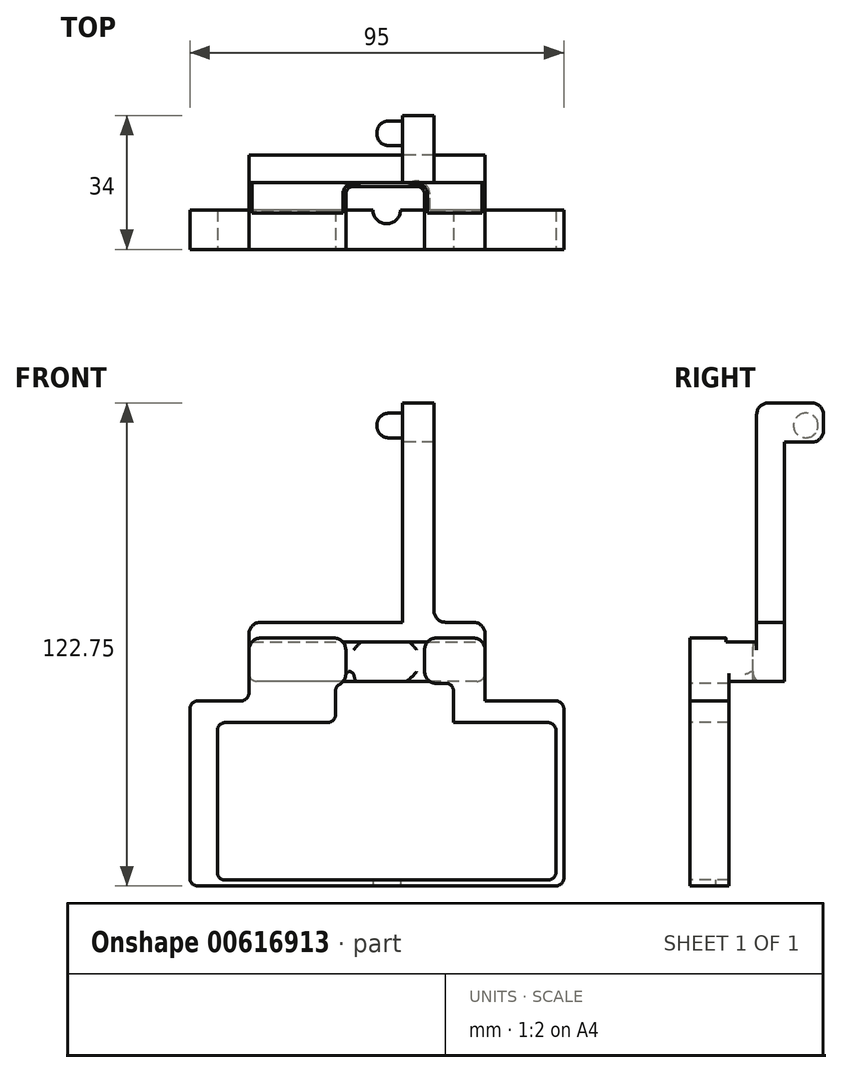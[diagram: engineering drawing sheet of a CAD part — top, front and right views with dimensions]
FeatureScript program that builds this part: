
annotation { "Feature Type Name" : "Feature", "Feature Type Description" : "" }
export const myFeature = defineFeature(function(context is Context, id is Id, definition is map)
    precondition{}
    {
        {
            var Q0;
            Q0=qCreatedBy(makeId("Front.planeOp"),FACE);
            var sketch = newSketch(context, id + "F0", { "sketchPlane" : qUnion([Q0])});
            skLineSegment(sketch, "E0.bottom", {"start": v(47.5, -23.5) * mm, "end": v(-47.5, -23.5) * mm});
            skLineSegment(sketch, "E0.top", {"start": v(47.5, 23.5) * mm, "end": v(-47.5, 23.5) * mm});
            skLineSegment(sketch, "E0.left", {"start": v(47.5, -23.5) * mm, "end": v(47.5, 23.5) * mm});
            skLineSegment(sketch, "E0.right", {"start": v(-47.5, -23.5) * mm, "end": v(-47.5, 23.5) * mm});
            skPoint(sketch, "E0.middle", {"position": v(0, 0) * mm});
            skSolve(sketch);
        }
        {
            var Q0;
            Q0=makeQuery(id+"F0.imprint","IMPRINT",FACE,{"disambiguationData":[TD([[makeQuery(id+"F0.imprint","IMPRINT",EDGE,{"derivedFrom":sQuery(id+"F0.wireOp",EDGE,"E0.bottom")}),-1.0]])]});
            extrude(context, id + "F1", {"entities" : qUnion([Q0]), "depth" : 1 * mm, "offsetDistance" : 25 * mm});
        }
        {
            var Q0;
            Q0=makeQuery(id+"F1.opExtrude","CAP_FACE",FACE,{"disambiguationData":[OSD([sQuery(id+"F0.wireOp",EDGE,"E0.bottom"),sQuery(id+"F0.wireOp",EDGE,"E0.top"),sQuery(id+"F0.wireOp",EDGE,"E0.left"),sQuery(id+"F0.wireOp",EDGE,"E0.right")])],"isStart":false});
            var sketch = newSketch(context, id + "F2", { "sketchPlane" : qUnion([Q0])});
            skLineSegment(sketch, "E1.bottom", {"start": v(-40.5, 18) * mm, "end": v(45.5, 18) * mm});
            skLineSegment(sketch, "E1.top", {"start": v(-40.5, -22) * mm, "end": v(45.5, -22) * mm});
            skLineSegment(sketch, "E1.left", {"start": v(-40.5, 18) * mm, "end": v(-40.5, -22) * mm});
            skLineSegment(sketch, "E1.right", {"start": v(45.5, 18) * mm, "end": v(45.5, -22) * mm});
            skLineSegment(sketch, "E2", {"start": v(2.5, -22) * mm, "end": v(2.5, -23.5) * mm});
            skLineSegment(sketch, "E3", {"start": v(45.5, 0) * mm, "end": v(47.5, 0) * mm});
            skLineSegment(sketch, "E4", {"start": v(-40.5, 0) * mm, "end": v(-47.5, 0) * mm});
            skLineSegment(sketch, "E5", {"start": v(32.76, 23.5) * mm, "end": v(32.76, 18) * mm});
            skSolve(sketch);
        }
        {
            var Q0;
            {var subQ4=sQuery(id+"F2.wireOp",EDGE,"E1.left");var subQ6=sQuery(id+"F2.wireOp",EDGE,"E1.bottom");var subQ9=makeQuery(id+"F2.imprint","INTERSECT",VERTEX,{"derivedFrom":[subQ6,subQ4]});Q0=makeQuery(id+"F2.imprint","IMPRINT",FACE,{"disambiguationData":[TD([[makeQuery(id+"F2.imprint","IMPRINT",EDGE,{"disambiguationData":[TD([[subQ9,-1.0]])],"derivedFrom":subQ6}),-1.0]])]});}
            extrude(context, id + "F3", {"entities" : qUnion([Q0]), "operationType" : NewBodyOperationType.REMOVE, "oppositeDirection" : true, "depth" : 25 * mm, "offsetDistance" : 25 * mm});
        }
        {
            var Q0;
            Q0=makeQuery(id+"F1.opExtrude","SWEPT_FACE",FACE,{"disambiguationData":[OSD([sQuery(id+"F0.wireOp",EDGE,"E0.top")])]});
            var sketch = newSketch(context, id + "F4", { "sketchPlane" : qUnion([Q0])});
            skLineSegment(sketch, "E6.bottom", {"start": v(27.5, 0) * mm, "end": v(-32.5, 0) * mm});
            skLineSegment(sketch, "E6.top", {"start": v(27.5, -1) * mm, "end": v(-32.5, -1) * mm});
            skLineSegment(sketch, "E6.left", {"start": v(27.5, 0) * mm, "end": v(27.5, -1) * mm});
            skLineSegment(sketch, "E6.right", {"start": v(-32.5, 0) * mm, "end": v(-32.5, -1) * mm});
            skLineSegment(sketch, "E7", {"start": v(47.5, -0.5) * mm, "end": v(27.5, -0.5) * mm});
            skSolve(sketch);
        }
        {
            var Q0;
            {var subQ4=sQuery(id+"F4.wireOp",EDGE,"E6.bottom");Q0=makeQuery(id+"F4.imprint","IMPRINT",FACE,{"disambiguationData":[TD([[makeQuery(id+"F4.imprint","IMPRINT",EDGE,{"derivedFrom":subQ4}),1.0]])]});}
            extrude(context, id + "F5", {"entities" : qUnion([Q0]), "operationType" : NewBodyOperationType.ADD, "depth" : 15 * mm, "offsetDistance" : 25 * mm});
        }
        {
            var Q0;
            Q0=makeQuery(id+"F5.boolean.opBoolean","MERGE",FACE,{"derivedFrom":[makeQuery(id+"F1.opExtrude","CAP_FACE",FACE,{"disambiguationData":[OSD([sQuery(id+"F0.wireOp",EDGE,"E0.bottom"),sQuery(id+"F0.wireOp",EDGE,"E0.top"),sQuery(id+"F0.wireOp",EDGE,"E0.left"),sQuery(id+"F0.wireOp",EDGE,"E0.right")])],"isStart":false}),makeQuery(id+"F5.opExtrude","SWEPT_FACE",FACE,{"disambiguationData":[OSD([sQuery(id+"F4.wireOp",EDGE,"E6.top")])]})]});
            var sketch = newSketch(context, id + "F6", { "sketchPlane" : qUnion([Q0])});
            skLineSegment(sketch, "E8.bottom", {"start": v(-10.5, 28) * mm, "end": v(19.5, 28) * mm});
            skLineSegment(sketch, "E8.top", {"start": v(-10.5, 18) * mm, "end": v(19.5, 18) * mm});
            skLineSegment(sketch, "E8.left", {"start": v(-10.5, 28) * mm, "end": v(-10.5, 18) * mm});
            skLineSegment(sketch, "E8.right", {"start": v(19.5, 28) * mm, "end": v(19.5, 18) * mm});
            skLineSegment(sketch, "E9", {"start": v(19.5, 26) * mm, "end": v(27.5, 26) * mm});
            skLineSegment(sketch, "E10", {"start": v(23.5, 26) * mm, "end": v(23.5, 18) * mm});
            skLineSegment(sketch, "E11", {"start": v(27.5, 23.5) * mm, "end": v(27.5, 18) * mm});
            skLineSegment(sketch, "E12.bottom", {"start": v(27.5, 39.25) * mm, "end": v(-32.5, 39.25) * mm});
            skLineSegment(sketch, "E12.top", {"start": v(27.5, 29.25) * mm, "end": v(-32.5, 29.25) * mm});
            skLineSegment(sketch, "E12.left", {"start": v(27.5, 39.25) * mm, "end": v(27.5, 29.25) * mm});
            skLineSegment(sketch, "E12.right", {"start": v(-32.5, 39.25) * mm, "end": v(-32.5, 29.25) * mm});
            skSolve(sketch);
        }
        {
            var Q0;
            {var subQ1=sQuery(id+"F6.wireOp",EDGE,"E8.bottom");Q0=makeQuery(id+"F6.imprint","IMPRINT",FACE,{"disambiguationData":[TD([[makeQuery(id+"F6.imprint","IMPRINT",EDGE,{"derivedFrom":subQ1}),-1.0]])]});}
            extrude(context, id + "F7", {"entities" : qUnion([Q0]), "operationType" : NewBodyOperationType.REMOVE, "oppositeDirection" : true, "depth" : 25 * mm, "offsetDistance" : 25 * mm});
        }
        {
            var Q0;
            Q0=makeQuery(id+"F6.imprint","IMPRINT",FACE,{"disambiguationData":[TD([[makeQuery(id+"F6.imprint","IMPRINT",EDGE,{"derivedFrom":sQuery(id+"F6.wireOp",EDGE,"E12.bottom")}),1.0]])]});
            extrude(context, id + "F8", {"entities" : qUnion([Q0]), "operationType" : NewBodyOperationType.REMOVE, "depth" : 2 * mm, "offsetDistance" : 25 * mm});
        }
        {
            var Q0;
            Q0=makeQuery(id+"F3.boolean.opBoolean","COPY",EDGE,{"derivedFrom":makeQuery(id+"F3.opExtrude","SWEPT_EDGE",EDGE,{"disambiguationData":[OSD([sQuery(id+"F2.wireOp",EDGE,"E1.top"),sQuery(id+"F2.wireOp",EDGE,"E1.left")])]})});
            var Q1;
            Q1=makeQuery(id+"F3.boolean.opBoolean","COPY",EDGE,{"derivedFrom":makeQuery(id+"F3.opExtrude","SWEPT_EDGE",EDGE,{"disambiguationData":[OSD([sQuery(id+"F2.wireOp",EDGE,"E1.top"),sQuery(id+"F2.wireOp",EDGE,"E1.right")])]})});
            var Q2;
            Q2=makeQuery(id+"F3.boolean.opBoolean","COPY",EDGE,{"derivedFrom":makeQuery(id+"F3.opExtrude","SWEPT_EDGE",EDGE,{"disambiguationData":[OSD([sQuery(id+"F2.wireOp",EDGE,"E1.bottom"),sQuery(id+"F2.wireOp",EDGE,"E1.right")])]})});
            var Q3;
            Q3=makeQuery(id+"F3.boolean.opBoolean","COPY",EDGE,{"derivedFrom":makeQuery(id+"F3.opExtrude","SWEPT_EDGE",EDGE,{"disambiguationData":[OSD([sQuery(id+"F2.wireOp",EDGE,"E1.bottom"),sQuery(id+"F2.wireOp",EDGE,"E1.left")])]})});
            var Q4;
            Q4=makeQuery(id+"F1.opExtrude","SWEPT_EDGE",EDGE,{"disambiguationData":[OSD([sQuery(id+"F0.wireOp",EDGE,"E0.bottom"),sQuery(id+"F0.wireOp",EDGE,"E0.right")])]});
            var Q5;
            Q5=makeQuery(id+"F1.opExtrude","SWEPT_EDGE",EDGE,{"disambiguationData":[OSD([sQuery(id+"F0.wireOp",EDGE,"E0.bottom"),sQuery(id+"F0.wireOp",EDGE,"E0.left")])]});
            var Q6;
            Q6=makeQuery(id+"F1.opExtrude","SWEPT_EDGE",EDGE,{"disambiguationData":[OSD([sQuery(id+"F0.wireOp",EDGE,"E0.top"),sQuery(id+"F0.wireOp",EDGE,"E0.right")])]});
            var Q7;
            Q7=makeQuery(id+"F5.opExtrude","CAP_EDGE",EDGE,{"disambiguationData":[OSD([sQuery(id+"F4.wireOp",EDGE,"E6.right")])],"isStart":true});
            var Q8;
            Q8=makeQuery(id+"F5.opExtrude","CAP_EDGE",EDGE,{"disambiguationData":[OSD([sQuery(id+"F4.wireOp",EDGE,"E6.left")])],"isStart":true});
            var Q9;
            Q9=makeQuery(id+"F1.opExtrude","SWEPT_EDGE",EDGE,{"disambiguationData":[OSD([sQuery(id+"F0.wireOp",EDGE,"E0.top"),sQuery(id+"F0.wireOp",EDGE,"E0.left")])]});
            var Q10;
            Q10=makeQuery(id+"F7.boolean.opBoolean","COPY",EDGE,{"derivedFrom":makeQuery(id+"F7.opExtrude","SWEPT_EDGE",EDGE,{"disambiguationData":[OSD([sQuery(id+"F2.wireOp",EDGE,"E1.bottom"),sQuery(id+"F6.wireOp",EDGE,"E8.top"),sQuery(id+"F6.wireOp",EDGE,"E8.left")])]})});
            var Q11;
            Q11=makeQuery(id+"F7.boolean.opBoolean","COPY",EDGE,{"derivedFrom":makeQuery(id+"F7.opExtrude","SWEPT_EDGE",EDGE,{"disambiguationData":[OSD([sQuery(id+"F6.wireOp",EDGE,"E8.bottom"),sQuery(id+"F6.wireOp",EDGE,"E8.left")])]})});
            var Q12;
            Q12=makeQuery(id+"F7.boolean.opBoolean","COPY",EDGE,{"derivedFrom":makeQuery(id+"F7.opExtrude","SWEPT_EDGE",EDGE,{"disambiguationData":[OSD([sQuery(id+"F2.wireOp",EDGE,"E1.bottom"),sQuery(id+"F6.wireOp",EDGE,"E8.top"),sQuery(id+"F6.wireOp",EDGE,"E8.right")])]})});
            var Q13;
            Q13=makeQuery(id+"F7.boolean.opBoolean","COPY",EDGE,{"derivedFrom":makeQuery(id+"F7.opExtrude","SWEPT_EDGE",EDGE,{"disambiguationData":[OSD([sQuery(id+"F6.wireOp",EDGE,"E8.bottom"),sQuery(id+"F6.wireOp",EDGE,"E8.right")])]})});
            fillet(context, id + "F9", {"entities" : qUnion([Q0, Q1, Q2, Q3, Q4, Q5, Q6, Q7, Q8, Q9, Q10, Q11, Q12, Q13]), "radius" : 2 * mm, "tangentPropagation" : true, "allowEdgeOverflow" : false});
        }
        {
            var Q0;
            Q0=makeQuery(id+"F5.boolean.opBoolean","MERGE",FACE,{"derivedFrom":[makeQuery(id+"F1.opExtrude","CAP_FACE",FACE,{"disambiguationData":[OSD([sQuery(id+"F0.wireOp",EDGE,"E0.bottom"),sQuery(id+"F0.wireOp",EDGE,"E0.top"),sQuery(id+"F0.wireOp",EDGE,"E0.left"),sQuery(id+"F0.wireOp",EDGE,"E0.right")])],"isStart":true}),makeQuery(id+"F5.opExtrude","SWEPT_FACE",FACE,{"disambiguationData":[OSD([sQuery(id+"F4.wireOp",EDGE,"E6.bottom")])]})]});
            var sketch = newSketch(context, id + "F10", { "sketchPlane" : qUnion([Q0])});
            skLineSegment(sketch, "E13.bottom", {"start": v(-27.5, 38.5) * mm, "end": v(32.5, 38.5) * mm});
            skLineSegment(sketch, "E13.top", {"start": v(-27.5, 28.5) * mm, "end": v(32.5, 28.5) * mm});
            skLineSegment(sketch, "E13.left", {"start": v(-27.5, 38.5) * mm, "end": v(-27.5, 28.5) * mm});
            skLineSegment(sketch, "E13.right", {"start": v(32.5, 38.5) * mm, "end": v(32.5, 28.5) * mm});
            skSolve(sketch);
        }
        {
            var Q0;
            Q0=makeQuery(id+"F10.imprint","IMPRINT",FACE,{"disambiguationData":[TD([[makeQuery(id+"F10.imprint","IMPRINT",EDGE,{"derivedFrom":sQuery(id+"F10.wireOp",EDGE,"E13.bottom")}),-1.0]])]});
            extrude(context, id + "F11", {"entities" : qUnion([Q0]), "operationType" : NewBodyOperationType.ADD, "depth" : 14 * mm, "offsetDistance" : 25 * mm});
        }
        {
            var Q0;
            Q0=makeQuery(id+"F11.boolean.opBoolean","MERGE",FACE,{"derivedFrom":[makeQuery(id+"F5.opExtrude","CAP_FACE",FACE,{"disambiguationData":[OSD([sQuery(id+"F4.wireOp",EDGE,"E6.bottom"),sQuery(id+"F4.wireOp",EDGE,"E6.top"),sQuery(id+"F4.wireOp",EDGE,"E6.left"),sQuery(id+"F4.wireOp",EDGE,"E6.right")])],"isStart":false}),makeQuery(id+"F11.opExtrude","SWEPT_FACE",FACE,{"disambiguationData":[OSD([sQuery(id+"F10.wireOp",EDGE,"E13.bottom")])]})]});
            var sketch = newSketch(context, id + "F12", { "sketchPlane" : qUnion([Q0])});
            skLineSegment(sketch, "E14.bottom", {"start": v(12.12, -1) * mm, "end": v(-7.88, -1) * mm});
            skLineSegment(sketch, "E14.top", {"start": v(12.12, 6) * mm, "end": v(-7.88, 6) * mm});
            skLineSegment(sketch, "E14.left", {"start": v(12.12, -1) * mm, "end": v(12.12, 6) * mm});
            skLineSegment(sketch, "E14.right", {"start": v(-7.88, -1) * mm, "end": v(-7.88, 6) * mm});
            skSolve(sketch);
        }
        {
            var Q0;
            Q0=makeQuery(id+"F12.imprint","IMPRINT",FACE,{"disambiguationData":[TD([[makeQuery(id+"F12.imprint","IMPRINT",EDGE,{"derivedFrom":sQuery(id+"F12.wireOp",EDGE,"E14.bottom")}),-1.0]])]});
            extrude(context, id + "F13", {"entities" : qUnion([Q0]), "operationType" : NewBodyOperationType.REMOVE, "oppositeDirection" : true, "depth" : 25 * mm, "offsetDistance" : 25 * mm});
        }
        {
            var Q0;
            Q0=makeQuery(id+"F11.opExtrude","SWEPT_EDGE",EDGE,{"disambiguationData":[OSD([sQuery(id+"F0.wireOp",EDGE,"E0.bottom"),sQuery(id+"F0.wireOp",EDGE,"E0.top"),sQuery(id+"F0.wireOp",EDGE,"E0.left"),sQuery(id+"F0.wireOp",EDGE,"E0.right"),sQuery(id+"F4.wireOp",EDGE,"E6.bottom"),sQuery(id+"F6.wireOp",EDGE,"E8.right"),sQuery(id+"F10.wireOp",EDGE,"E13.top")])]});
            var Q1;
            Q1=makeQuery(id+"F11.opExtrude","SWEPT_EDGE",EDGE,{"disambiguationData":[OSD([sQuery(id+"F0.wireOp",EDGE,"E0.bottom"),sQuery(id+"F0.wireOp",EDGE,"E0.top"),sQuery(id+"F0.wireOp",EDGE,"E0.left"),sQuery(id+"F0.wireOp",EDGE,"E0.right"),sQuery(id+"F4.wireOp",EDGE,"E6.bottom"),sQuery(id+"F6.wireOp",EDGE,"E8.left"),sQuery(id+"F10.wireOp",EDGE,"E13.top")])]});
            var Q2;
            Q2=makeQuery(id+"F11.opExtrude","SWEPT_EDGE",EDGE,{"disambiguationData":[OSD([sQuery(id+"F10.wireOp",EDGE,"E13.top"),sQuery(id+"F10.wireOp",EDGE,"E13.right")])]});
            var Q3;
            Q3=makeQuery(id+"F11.opExtrude","SWEPT_EDGE",EDGE,{"disambiguationData":[OSD([sQuery(id+"F10.wireOp",EDGE,"E13.top"),sQuery(id+"F10.wireOp",EDGE,"E13.left")])]});
            var Q4;
            Q4=makeQuery(id+"F13.boolean.opBoolean","COPY",EDGE,{"derivedFrom":makeQuery(id+"F13.opExtrude","SWEPT_EDGE",EDGE,{"disambiguationData":[OSD([sQuery(id+"F12.wireOp",EDGE,"E14.top"),sQuery(id+"F12.wireOp",EDGE,"E14.left")])]})});
            var Q5;
            Q5=makeQuery(id+"F13.boolean.opBoolean","COPY",EDGE,{"derivedFrom":makeQuery(id+"F13.opExtrude","SWEPT_EDGE",EDGE,{"disambiguationData":[OSD([sQuery(id+"F12.wireOp",EDGE,"E14.top"),sQuery(id+"F12.wireOp",EDGE,"E14.right")])]})});
            fillet(context, id + "F14", {"entities" : qUnion([Q0, Q1, Q2, Q3, Q4, Q5]), "radius" : 2 * mm, "tangentPropagation" : true, "allowEdgeOverflow" : false});
        }
        {
            var Q0;
            Q0=makeQuery(id+"F11.boolean.opBoolean","MERGE",FACE,{"derivedFrom":[makeQuery(id+"F5.opExtrude","CAP_FACE",FACE,{"disambiguationData":[OSD([sQuery(id+"F4.wireOp",EDGE,"E6.bottom"),sQuery(id+"F4.wireOp",EDGE,"E6.top"),sQuery(id+"F4.wireOp",EDGE,"E6.left"),sQuery(id+"F4.wireOp",EDGE,"E6.right")])],"isStart":false}),makeQuery(id+"F11.opExtrude","SWEPT_FACE",FACE,{"disambiguationData":[OSD([sQuery(id+"F10.wireOp",EDGE,"E13.bottom")])]})]});
            var sketch = newSketch(context, id + "F15", { "sketchPlane" : qUnion([Q0])});
            skLineSegment(sketch, "E15", {"start": v(-32.5, 3.2) * mm, "end": v(1.5, 3.2) * mm});
            skLineSegment(sketch, "E16.bottom", {"start": v(-32.5, -1) * mm, "end": v(-7.88, -1) * mm});
            skLineSegment(sketch, "E16.top", {"start": v(-32.5, 0) * mm, "end": v(-7.88, 0) * mm});
            skLineSegment(sketch, "E16.left", {"start": v(-32.5, -1) * mm, "end": v(-32.5, 0) * mm});
            skLineSegment(sketch, "E16.right", {"start": v(-7.88, -1) * mm, "end": v(-7.88, 0) * mm});
            skLineSegment(sketch, "E17.bottom", {"start": v(12.12, -1) * mm, "end": v(27.5, -1) * mm});
            skLineSegment(sketch, "E17.top", {"start": v(12.12, 0) * mm, "end": v(27.5, 0) * mm});
            skLineSegment(sketch, "E17.left", {"start": v(12.12, -1) * mm, "end": v(12.12, 0) * mm});
            skLineSegment(sketch, "E17.right", {"start": v(27.5, -1) * mm, "end": v(27.5, 0) * mm});
            skLineSegment(sketch, "E18", {"start": v(-32.5, 0) * mm, "end": v(-32.5, 7) * mm});
            skLineSegment(sketch, "E19.bottom", {"start": v(-32.5, 7) * mm, "end": v(27.5, 7) * mm});
            skLineSegment(sketch, "E19.top", {"start": v(-32.5, 14) * mm, "end": v(27.5, 14) * mm});
            skLineSegment(sketch, "E19.left", {"start": v(-32.5, 7) * mm, "end": v(-32.5, 14) * mm});
            skLineSegment(sketch, "E19.right", {"start": v(27.5, 7) * mm, "end": v(27.5, 14) * mm});
            skSolve(sketch);
        }
        {
            var Q0;
            Q0=makeQuery(id+"F15.imprint","IMPRINT",FACE,{"disambiguationData":[TD([[makeQuery(id+"F15.imprint","IMPRINT",EDGE,{"derivedFrom":sQuery(id+"F15.wireOp",EDGE,"E17.bottom")}),-1.0]])]});
            var Q1;
            Q1=makeQuery(id+"F15.imprint","IMPRINT",FACE,{"disambiguationData":[TD([[makeQuery(id+"F15.imprint","IMPRINT",EDGE,{"derivedFrom":sQuery(id+"F15.wireOp",EDGE,"E16.bottom")}),-1.0]])]});
            extrude(context, id + "F16", {"entities" : qUnion([Q0, Q1]), "operationType" : NewBodyOperationType.ADD, "depth" : 1 * mm, "offsetDistance" : 25 * mm});
        }
        {
            var Q0;
            Q0=makeQuery(id+"F15.imprint","IMPRINT",FACE,{"disambiguationData":[TD([[makeQuery(id+"F15.imprint","IMPRINT",EDGE,{"derivedFrom":sQuery(id+"F15.wireOp",EDGE,"E19.bottom")}),1.0]])]});
            extrude(context, id + "F17", {"entities" : qUnion([Q0]), "operationType" : NewBodyOperationType.ADD, "depth" : 5 * mm, "offsetDistance" : 25 * mm});
        }
        {
            var Q0;
            Q0=makeQuery(id+"F17.opExtrude","CAP_FACE",FACE,{"disambiguationData":[OSD([sQuery(id+"F15.wireOp",EDGE,"E19.bottom"),sQuery(id+"F15.wireOp",EDGE,"E19.top"),sQuery(id+"F15.wireOp",EDGE,"E19.left"),sQuery(id+"F15.wireOp",EDGE,"E19.right")])],"isStart":false});
            var sketch = newSketch(context, id + "F18", { "sketchPlane" : qUnion([Q0])});
            skLineSegment(sketch, "E20.bottom", {"start": v(6.5, 14) * mm, "end": v(14.5, 14) * mm});
            skLineSegment(sketch, "E20.top", {"start": v(6.5, 7) * mm, "end": v(14.5, 7) * mm});
            skLineSegment(sketch, "E20.left", {"start": v(6.5, 14) * mm, "end": v(6.5, 7) * mm});
            skLineSegment(sketch, "E20.right", {"start": v(14.5, 14) * mm, "end": v(14.5, 7) * mm});
            skLineSegment(sketch, "E21", {"start": v(-32.5, 10.5) * mm, "end": v(6.5, 10.5) * mm});
            skLineSegment(sketch, "E22", {"start": v(6.5, 10.5) * mm, "end": v(14.5, 10.5) * mm});
            skSolve(sketch);
        }
        {
            var Q0;
            {var subQ0=sQuery(id+"F18.wireOp",EDGE,"E20.top");Q0=makeQuery(id+"F18.imprint","IMPRINT",FACE,{"disambiguationData":[TD([[makeQuery(id+"F18.imprint","IMPRINT",EDGE,{"derivedFrom":subQ0}),1.0]])]});}
            var Q1;
            {var subQ0=sQuery(id+"F18.wireOp",EDGE,"E20.bottom");Q1=makeQuery(id+"F18.imprint","IMPRINT",FACE,{"disambiguationData":[TD([[makeQuery(id+"F18.imprint","IMPRINT",EDGE,{"derivedFrom":subQ0}),1.0]])]});}
            extrude(context, id + "F19", {"entities" : qUnion([Q0, Q1]), "operationType" : NewBodyOperationType.ADD, "depth" : 55.75 * mm, "offsetDistance" : 25 * mm});
        }
        {
            var Q0;
            Q0=makeQuery(id+"F19.boolean.opBoolean","MERGE",FACE,{"derivedFrom":[makeQuery(id+"F17.boolean.opBoolean","MERGE",FACE,{"derivedFrom":[makeQuery(id+"F11.opExtrude","CAP_FACE",FACE,{"disambiguationData":[OSD([sQuery(id+"F10.wireOp",EDGE,"E13.bottom"),sQuery(id+"F10.wireOp",EDGE,"E13.top"),sQuery(id+"F10.wireOp",EDGE,"E13.left"),sQuery(id+"F10.wireOp",EDGE,"E13.right")])],"isStart":false}),makeQuery(id+"F17.opExtrude","SWEPT_FACE",FACE,{"disambiguationData":[OSD([sQuery(id+"F15.wireOp",EDGE,"E19.top")])]})]}),makeQuery(id+"F19.opExtrude","SWEPT_FACE",FACE,{"disambiguationData":[OSD([sQuery(id+"F18.wireOp",EDGE,"E20.bottom")])]})]});
            var sketch = newSketch(context, id + "F20", { "sketchPlane" : qUnion([Q0])});
            skLineSegment(sketch, "E23.bottom", {"start": v(-14.5, 99.25) * mm, "end": v(-6.5, 99.25) * mm});
            skLineSegment(sketch, "E23.top", {"start": v(-14.5, 89.25) * mm, "end": v(-6.5, 89.25) * mm});
            skLineSegment(sketch, "E23.left", {"start": v(-14.5, 99.25) * mm, "end": v(-14.5, 89.25) * mm});
            skLineSegment(sketch, "E23.right", {"start": v(-6.5, 99.25) * mm, "end": v(-6.5, 89.25) * mm});
            skSolve(sketch);
        }
        {
            var Q0;
            Q0=makeQuery(id+"F20.imprint","IMPRINT",FACE,{"disambiguationData":[TD([[makeQuery(id+"F20.imprint","IMPRINT",EDGE,{"derivedFrom":sQuery(id+"F20.wireOp",EDGE,"E23.bottom")}),-1.0]])]});
            var Q1;
            Q1 = qSketchRegion(id + "F22", true);
            extrude(context, id + "F21", {"entities" : qUnion([Q0, Q1]), "operationType" : NewBodyOperationType.ADD, "depth" : 10 * mm, "offsetDistance" : 25 * mm});
        }
        {
            var Q0;
            Q0=makeQuery(id+"F21.boolean.opBoolean","MERGE",FACE,{"derivedFrom":[makeQuery(id+"F19.opExtrude","SWEPT_FACE",FACE,{"disambiguationData":[OSD([sQuery(id+"F18.wireOp",EDGE,"E20.left")])]}),makeQuery(id+"F21.opExtrude","SWEPT_FACE",FACE,{"disambiguationData":[OSD([sQuery(id+"F20.wireOp",EDGE,"E23.right")])]})]});
            var sketch = newSketch(context, id + "F22", { "sketchPlane" : qUnion([Q0])});
            skCircle(sketch, "E24", {"center": v(-19.5, 93.5) * mm, "radius": 3.12 * mm});
            skLineSegment(sketch, "E25", {"start": v(-10.5, 43.5) * mm, "end": v(-10.5, 93.5) * mm});
            skLineSegment(sketch, "E26", {"start": v(-10.5, 93.5) * mm, "end": v(-10.5, 99.25) * mm});
            skLineSegment(sketch, "E27", {"start": v(-19.5, 93.5) * mm, "end": v(-19.5, 99.25) * mm});
            skLineSegment(sketch, "E28", {"start": v(-14, 89.25) * mm, "end": v(-14, 99.25) * mm});
            skLineSegment(sketch, "E29", {"start": v(-19.5, 93.5) * mm, "end": v(-14, 93.5) * mm});
            skLineSegment(sketch, "E30", {"start": v(-16.75, 93.5) * mm, "end": v(-16.75, 89.25) * mm});
            skSolve(sketch);
        }
        {
            var Q0;
            Q0 = qSketchRegion(id + "F22", true);
            extrude(context, id + "F23", {"entities" : qUnion([Q0]), "operationType" : NewBodyOperationType.ADD, "depth" : 6.5 * mm, "offsetDistance" : 25 * mm});
        }
        {
            var Q0;
            Q0=makeQuery(id+"F16.boolean.opBoolean","MERGE",FACE,{"derivedFrom":[makeQuery(id+"F5.boolean.opBoolean","MERGE",FACE,{"derivedFrom":[makeQuery(id+"F1.opExtrude","CAP_FACE",FACE,{"disambiguationData":[OSD([sQuery(id+"F0.wireOp",EDGE,"E0.bottom"),sQuery(id+"F0.wireOp",EDGE,"E0.top"),sQuery(id+"F0.wireOp",EDGE,"E0.left"),sQuery(id+"F0.wireOp",EDGE,"E0.right")])],"isStart":false}),makeQuery(id+"F5.opExtrude","SWEPT_FACE",FACE,{"disambiguationData":[OSD([sQuery(id+"F4.wireOp",EDGE,"E6.top")])]})]}),makeQuery(id+"F16.opExtrude","SWEPT_FACE",FACE,{"disambiguationData":[OSD([sQuery(id+"F15.wireOp",EDGE,"E16.bottom")])]}),makeQuery(id+"F16.opExtrude","SWEPT_FACE",FACE,{"disambiguationData":[OSD([sQuery(id+"F15.wireOp",EDGE,"E17.bottom")])]})]});
            var sketch = newSketch(context, id + "F24", { "sketchPlane" : qUnion([Q0])});
            skSolve(sketch);
        }
        {
            var Q0;
            Q0 = qSketchRegion(id + "F24", true);
            var Q1;
            {var subQ6=sQuery(id+"F0.wireOp",EDGE,"E0.bottom");Q1=makeQuery(id+"F24.imprint","IMPRINT",FACE,{"disambiguationData":[TD([[makeQuery(id+"F24.imprint","IMPRINT",EDGE,{"derivedFrom":makeQuery(id+"F1.opExtrude","CAP_EDGE",EDGE,{"disambiguationData":[OSD([subQ6])],"isStart":false})}),-1.0]])]});}
            extrude(context, id + "F25", {"entities" : qUnion([Q0, Q1]), "operationType" : NewBodyOperationType.ADD, "depth" : 9 * mm, "offsetDistance" : 25 * mm});
        }
        {
            var Q0;
            Q0=makeQuery(id+"F16.opExtrude","SWEPT_FACE",FACE,{"disambiguationData":[OSD([sQuery(id+"F15.wireOp",EDGE,"E16.top")])]});
            var sketch = newSketch(context, id + "F26", { "sketchPlane" : qUnion([Q0])});
            skSolve(sketch);
        }
        {
            var Q0;
            {var subQ0=sQuery(id+"F15.wireOp",EDGE,"E16.top");Q0=makeQuery(id+"F26.imprint","IMPRINT",FACE,{"disambiguationData":[TD([[makeQuery(id+"F26.imprint","IMPRINT",EDGE,{"derivedFrom":makeQuery(id+"F16.opExtrude","CAP_EDGE",EDGE,{"disambiguationData":[OSD([subQ0])],"isStart":false})}),1.0]])]});}
            var Q1;
            Q1=makeQuery(id+"F16.opExtrude","SWEPT_FACE",FACE,{"disambiguationData":[OSD([sQuery(id+"F15.wireOp",EDGE,"E17.top")])]});
            extrude(context, id + "F27", {"entities" : qUnion([Q0, Q1]), "operationType" : NewBodyOperationType.REMOVE, "oppositeDirection" : true, "depth" : .75 * mm, "offsetDistance" : 25 * mm});
        }
        {
            var Q0;
            Q0=makeQuery(id+"F23.opExtrude","CAP_EDGE",EDGE,{"disambiguationData":[OSD([sQuery(id+"F22.wireOp",EDGE,"E24")])],"isStart":false});
            var Q1;
            Q1=makeQuery(id+"F19.opExtrude","CAP_EDGE",EDGE,{"disambiguationData":[OSD([sQuery(id+"F18.wireOp",EDGE,"E20.top")])],"isStart":false});
            var Q2;
            Q2=makeQuery(id+"F21.opExtrude","CAP_EDGE",EDGE,{"disambiguationData":[OSD([sQuery(id+"F20.wireOp",EDGE,"E23.bottom")])],"isStart":false});
            var Q3;
            {var subQ0=sQuery(id+"F15.wireOp",EDGE,"E16.left");Q3=makeQuery(id+"F25.boolean.opBoolean","MERGE",EDGE,{"derivedFrom":[makeQuery(id+"F16.opExtrude","CAP_EDGE",EDGE,{"disambiguationData":[OSD([subQ0])],"isStart":false}),makeQuery(id+"F25.opExtrude","SWEPT_EDGE",EDGE,{"disambiguationData":[OSD([sQuery(id+"F0.wireOp",EDGE,"E0.top"),sQuery(id+"F4.wireOp",EDGE,"E6.top"),sQuery(id+"F4.wireOp",EDGE,"E6.right"),sQuery(id+"F15.wireOp",EDGE,"E16.bottom"),subQ0])]})]});}
            var Q4;
            {var subQ0=sQuery(id+"F15.wireOp",EDGE,"E16.right");Q4=makeQuery(id+"F25.boolean.opBoolean","MERGE",EDGE,{"derivedFrom":[makeQuery(id+"F16.opExtrude","CAP_EDGE",EDGE,{"disambiguationData":[OSD([subQ0])],"isStart":false}),makeQuery(id+"F25.opExtrude","SWEPT_EDGE",EDGE,{"disambiguationData":[OSD([sQuery(id+"F4.wireOp",EDGE,"E6.top"),sQuery(id+"F12.wireOp",EDGE,"E14.bottom"),sQuery(id+"F12.wireOp",EDGE,"E14.right"),sQuery(id+"F15.wireOp",EDGE,"E16.bottom"),subQ0])]})]});}
            var Q5;
            {var subQ0=sQuery(id+"F15.wireOp",EDGE,"E17.left");Q5=makeQuery(id+"F25.boolean.opBoolean","MERGE",EDGE,{"derivedFrom":[makeQuery(id+"F16.opExtrude","CAP_EDGE",EDGE,{"disambiguationData":[OSD([subQ0])],"isStart":false}),makeQuery(id+"F25.opExtrude","SWEPT_EDGE",EDGE,{"disambiguationData":[OSD([sQuery(id+"F4.wireOp",EDGE,"E6.top"),sQuery(id+"F12.wireOp",EDGE,"E14.bottom"),sQuery(id+"F12.wireOp",EDGE,"E14.left"),sQuery(id+"F15.wireOp",EDGE,"E17.bottom"),subQ0])]})]});}
            var Q6;
            {var subQ0=sQuery(id+"F15.wireOp",EDGE,"E17.right");Q6=makeQuery(id+"F25.boolean.opBoolean","MERGE",EDGE,{"derivedFrom":[makeQuery(id+"F16.opExtrude","CAP_EDGE",EDGE,{"disambiguationData":[OSD([subQ0])],"isStart":false}),makeQuery(id+"F25.opExtrude","SWEPT_EDGE",EDGE,{"disambiguationData":[OSD([sQuery(id+"F0.wireOp",EDGE,"E0.top"),sQuery(id+"F4.wireOp",EDGE,"E6.top"),sQuery(id+"F4.wireOp",EDGE,"E6.left"),sQuery(id+"F15.wireOp",EDGE,"E17.bottom"),subQ0])]})]});}
            var Q7;
            {var subQ0=sQuery(id+"F12.wireOp",EDGE,"E14.left");var subQ1=sQuery(id+"F6.wireOp",EDGE,"E8.bottom");Q7=makeQuery(id+"F25.boolean.opBoolean","MERGE",EDGE,{"derivedFrom":[makeQuery(id+"F13.boolean.opBoolean","INTERSECT",EDGE,{"derivedFrom":[makeQuery(id+"F7.boolean.opBoolean","COPY",FACE,{"derivedFrom":makeQuery(id+"F7.opExtrude","SWEPT_FACE",FACE,{"disambiguationData":[OSD([subQ1])]})}),makeQuery(id+"F13.opExtrude","SWEPT_FACE",FACE,{"disambiguationData":[OSD([subQ0])]})]}),makeQuery(id+"F25.opExtrude","SWEPT_EDGE",EDGE,{"disambiguationData":[OSD([sQuery(id+"F4.wireOp",EDGE,"E6.top"),subQ1,sQuery(id+"F12.wireOp",EDGE,"E14.bottom"),subQ0,sQuery(id+"F15.wireOp",EDGE,"E17.bottom"),sQuery(id+"F15.wireOp",EDGE,"E17.left")])]})]});}
            var Q8;
            {var subQ0=sQuery(id+"F12.wireOp",EDGE,"E14.right");var subQ1=sQuery(id+"F6.wireOp",EDGE,"E8.bottom");Q8=makeQuery(id+"F25.boolean.opBoolean","MERGE",EDGE,{"derivedFrom":[makeQuery(id+"F13.boolean.opBoolean","INTERSECT",EDGE,{"derivedFrom":[makeQuery(id+"F7.boolean.opBoolean","COPY",FACE,{"derivedFrom":makeQuery(id+"F7.opExtrude","SWEPT_FACE",FACE,{"disambiguationData":[OSD([subQ1])]})}),makeQuery(id+"F13.opExtrude","SWEPT_FACE",FACE,{"disambiguationData":[OSD([subQ0])]})]}),makeQuery(id+"F25.opExtrude","SWEPT_EDGE",EDGE,{"disambiguationData":[OSD([sQuery(id+"F4.wireOp",EDGE,"E6.top"),subQ1,sQuery(id+"F12.wireOp",EDGE,"E14.bottom"),subQ0,sQuery(id+"F15.wireOp",EDGE,"E16.bottom"),sQuery(id+"F15.wireOp",EDGE,"E16.right")])]})]});}
            var Q9;
            Q9=makeQuery(id+"F17.opExtrude","CAP_EDGE",EDGE,{"disambiguationData":[OSD([sQuery(id+"F15.wireOp",EDGE,"E19.left")])],"isStart":false});
            var Q10;
            Q10=makeQuery(id+"F17.opExtrude","CAP_EDGE",EDGE,{"disambiguationData":[OSD([sQuery(id+"F15.wireOp",EDGE,"E19.right")])],"isStart":false});
            var Q11;
            Q11=makeQuery(id+"F21.opExtrude","CAP_EDGE",EDGE,{"disambiguationData":[OSD([sQuery(id+"F20.wireOp",EDGE,"E23.top")])],"isStart":false});
            var Q12;
            Q12=makeQuery(id+"F21.opExtrude","CAP_EDGE",EDGE,{"disambiguationData":[OSD([sQuery(id+"F20.wireOp",EDGE,"E23.top")])],"isStart":true});
            var Q13;
            Q13=makeQuery(id+"F19.opExtrude","CAP_EDGE",EDGE,{"disambiguationData":[OSD([sQuery(id+"F18.wireOp",EDGE,"E20.left")])],"isStart":true});
            var Q14;
            Q14=makeQuery(id+"F19.opExtrude","CAP_EDGE",EDGE,{"disambiguationData":[OSD([sQuery(id+"F18.wireOp",EDGE,"E20.right")])],"isStart":true});
            fillet(context, id + "F28", {"entities" : qUnion([Q0, Q1, Q2, Q3, Q4, Q5, Q6, Q7, Q8, Q9, Q10, Q11, Q12, Q13, Q14]), "radius" : 3 * mm, "tangentPropagation" : true, "allowEdgeOverflow" : false});
        }
        {
            var Q0;
            {var subQ0=sQuery(id+"F0.wireOp",EDGE,"E0.bottom");Q0=makeQuery(id+"F25.boolean.opBoolean","MERGE",FACE,{"derivedFrom":[makeQuery(id+"F1.opExtrude","SWEPT_FACE",FACE,{"disambiguationData":[OSD([subQ0])]}),makeQuery(id+"F25.opExtrude","SWEPT_FACE",FACE,{"disambiguationData":[OSD([subQ0])]})]});}
            var sketch = newSketch(context, id + "F29", { "sketchPlane" : qUnion([Q0])});
            skLineSegment(sketch, "E31", {"start": v(45.5, 5) * mm, "end": v(2.5, 5) * mm});
            skPoint(sketch, "E31.endSnap0", {"position": v(45.5, 5) * mm});
            skLineSegment(sketch, "E32", {"start": v(2.5, 5) * mm, "end": v(2.5, 0) * mm});
            skCircle(sketch, "E33", {"center": v(2.5, 0) * mm, "radius": 3.5 * mm});
            skSolve(sketch);
        }
        {
            var Q0;
            Q0 = qSketchRegion(id + "F29", true);
            extrude(context, id + "F30", {"entities" : qUnion([Q0]), "operationType" : NewBodyOperationType.REMOVE, "oppositeDirection" : true, "depth" : 25 * mm, "offsetDistance" : 25 * mm});
        }
    });
